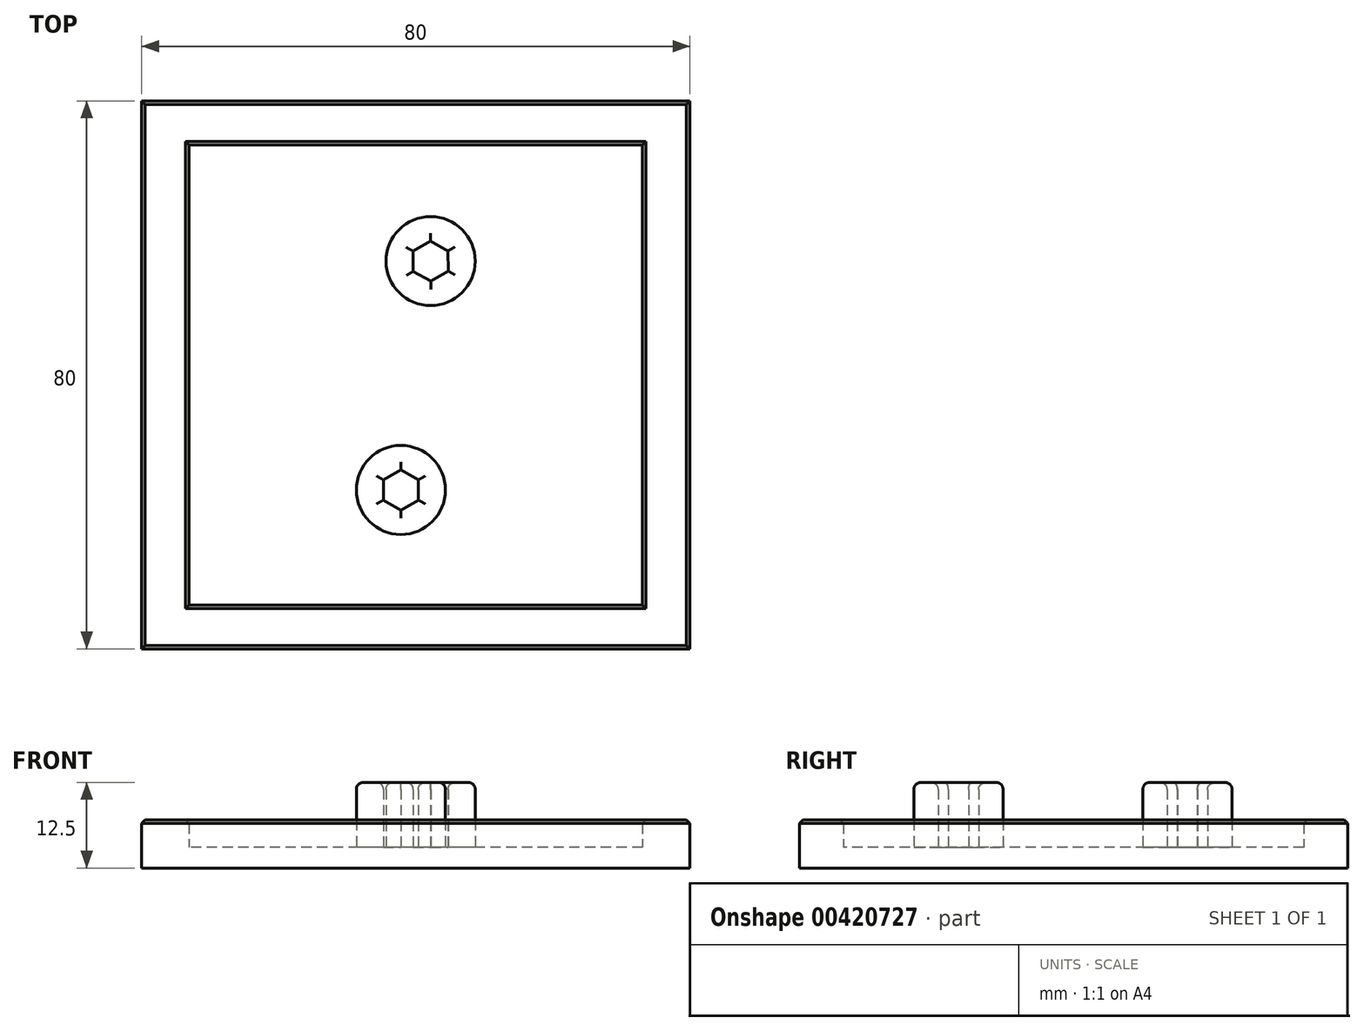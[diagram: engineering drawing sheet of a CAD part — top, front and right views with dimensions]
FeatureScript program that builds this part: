
annotation { "Feature Type Name" : "Feature", "Feature Type Description" : "" }
export const myFeature = defineFeature(function(context is Context, id is Id, definition is map)
    precondition{}
    {
        {
            var Q0;
            Q0=qCreatedBy(makeId("Top.planeOp"),FACE);
            var sketch = newSketch(context, id + "F0", { "sketchPlane" : qUnion([Q0])});
            skLineSegment(sketch, "E0.bottom", {"start": v(40, 40) * mm, "end": v(-40, 40) * mm});
            skLineSegment(sketch, "E0.top", {"start": v(40, -40) * mm, "end": v(-40, -40) * mm});
            skLineSegment(sketch, "E0.left", {"start": v(40, 40) * mm, "end": v(40, -40) * mm});
            skLineSegment(sketch, "E0.right", {"start": v(-40, 40) * mm, "end": v(-40, -40) * mm});
            skPoint(sketch, "E0.middle", {"position": v(0, 0) * mm});
            skCircle(sketch, "E1.cCircle", {"center": v(2.17, 16.62) * mm, "radius": 2.55 * mm, "construction": true});
            skLineSegment(sketch, "E1.0", {"start": v(2.15, 19.56) * mm, "end": v(4.7, 18.1) * mm});
            skLineSegment(sketch, "E1.1", {"start": v(4.7, 18.1) * mm, "end": v(4.73, 15.17) * mm});
            skLineSegment(sketch, "E1.2", {"start": v(4.73, 15.17) * mm, "end": v(2.2, 13.67) * mm});
            skLineSegment(sketch, "E1.3", {"start": v(2.2, 13.67) * mm, "end": v(-0.37, 15.12) * mm});
            skLineSegment(sketch, "E1.4", {"start": v(-0.37, 15.12) * mm, "end": v(-0.4, 18.07) * mm});
            skLineSegment(sketch, "E1.5", {"start": v(-0.4, 18.07) * mm, "end": v(2.15, 19.56) * mm});
            skPoint(sketch, "E1.0.midPoint", {"position": v(3.43, 18.84) * mm});
            skCircle(sketch, "E2", {"center": v(2.17, 16.62) * mm, "radius": 6.5 * mm});
            skCircle(sketch, "E3.cCircle", {"center": v(-2.17, -16.8) * mm, "radius": 2.55 * mm, "construction": true});
            skLineSegment(sketch, "E3.0", {"start": v(0.38, -15.33) * mm, "end": v(0.38, -18.27) * mm});
            skLineSegment(sketch, "E3.1", {"start": v(0.38, -18.27) * mm, "end": v(-2.17, -19.74) * mm});
            skLineSegment(sketch, "E3.2", {"start": v(-2.17, -19.74) * mm, "end": v(-4.72, -18.27) * mm});
            skLineSegment(sketch, "E3.3", {"start": v(-4.72, -18.27) * mm, "end": v(-4.72, -15.33) * mm});
            skLineSegment(sketch, "E3.4", {"start": v(-4.72, -15.33) * mm, "end": v(-2.17, -13.86) * mm});
            skLineSegment(sketch, "E3.5", {"start": v(-2.17, -13.86) * mm, "end": v(0.38, -15.33) * mm});
            skPoint(sketch, "E3.0.midPoint", {"position": v(0.38, -16.8) * mm});
            skCircle(sketch, "E4", {"center": v(-2.17, -16.8) * mm, "radius": 6.5 * mm});
            skSolve(sketch);
        }
        {
            var Q0;
            Q0=makeQuery(id+"F0.imprint","IMPRINT",FACE,{"disambiguationData":[TD([[makeQuery(id+"F0.imprint","IMPRINT",EDGE,{"derivedFrom":sQuery(id+"F0.wireOp",EDGE,"E0.bottom")}),1.0]])]});
            var Q1;
            Q1=makeQuery(id+"F0.imprint","IMPRINT",FACE,{"disambiguationData":[TD([[makeQuery(id+"F0.imprint","IMPRINT",EDGE,{"derivedFrom":sQuery(id+"F0.wireOp",EDGE,"E1.0")}),1.0]])]});
            var Q2;
            Q2=makeQuery(id+"F0.imprint","IMPRINT",FACE,{"disambiguationData":[TD([[makeQuery(id+"F0.imprint","IMPRINT",EDGE,{"derivedFrom":sQuery(id+"F0.wireOp",EDGE,"E1.0")}),-1.0]])]});
            var Q3;
            Q3=makeQuery(id+"F0.imprint","IMPRINT",FACE,{"disambiguationData":[TD([[makeQuery(id+"F0.imprint","IMPRINT",EDGE,{"derivedFrom":sQuery(id+"F0.wireOp",EDGE,"gQONg82r-pYZi-LkUd-rfeB-qmEZ9qJ01gSx")}),-1.0]])]});
            var Q4;
            Q4=makeQuery(id+"F0.imprint","IMPRINT",FACE,{"disambiguationData":[TD([[makeQuery(id+"F0.imprint","IMPRINT",EDGE,{"derivedFrom":sQuery(id+"F0.wireOp",EDGE,"gQONg82r-pYZi-LkUd-rfeB-qmEZ9qJ01gSx")}),1.0]])]});
            var Q5;
            Q5=makeQuery(id+"F0.imprint","IMPRINT",FACE,{"disambiguationData":[TD([[makeQuery(id+"F0.imprint","IMPRINT",EDGE,{"derivedFrom":sQuery(id+"F0.wireOp",EDGE,"rSCinz5W-PWQ1-Tyf3-0WCw-5ZFN2yuS5qdL")}),1.0]])]});
            var Q6;
            Q6=makeQuery(id+"F0.imprint","IMPRINT",FACE,{"disambiguationData":[TD([[makeQuery(id+"F0.imprint","IMPRINT",EDGE,{"derivedFrom":sQuery(id+"F0.wireOp",EDGE,"rSCinz5W-PWQ1-Tyf3-0WCw-5ZFN2yuS5qdL")}),-1.0]])]});
            var Q7;
            Q7=makeQuery(id+"F0.imprint","IMPRINT",FACE,{"disambiguationData":[TD([[makeQuery(id+"F0.imprint","IMPRINT",EDGE,{"derivedFrom":sQuery(id+"F0.wireOp",EDGE,"PcAE5poN-MP8w-SmH2-FwNS-jAMijU5FzXcH")}),1.0]])]});
            var Q8;
            Q8=makeQuery(id+"F0.imprint","IMPRINT",FACE,{"disambiguationData":[TD([[makeQuery(id+"F0.imprint","IMPRINT",EDGE,{"derivedFrom":sQuery(id+"F0.wireOp",EDGE,"E3.0")}),1.0]])]});
            var Q9;
            Q9=makeQuery(id+"F0.imprint","IMPRINT",FACE,{"disambiguationData":[TD([[makeQuery(id+"F0.imprint","IMPRINT",EDGE,{"derivedFrom":sQuery(id+"F0.wireOp",EDGE,"E3.0")}),-1.0]])]});
            extrude(context, id + "F1", {"entities" : qUnion([Q0, Q1, Q2, Q3, Q4, Q5, Q6, Q7, Q8, Q9]), "depth" : 3 * mm});
        }
        {
            var Q0;
            Q0=makeQuery(id+"F0.imprint","IMPRINT",FACE,{"disambiguationData":[TD([[makeQuery(id+"F0.imprint","IMPRINT",EDGE,{"derivedFrom":sQuery(id+"F0.wireOp",EDGE,"rSCinz5W-PWQ1-Tyf3-0WCw-5ZFN2yuS5qdL")}),-1.0]])]});
            var Q1;
            Q1=makeQuery(id+"F0.imprint","IMPRINT",FACE,{"disambiguationData":[TD([[makeQuery(id+"F0.imprint","IMPRINT",EDGE,{"derivedFrom":sQuery(id+"F0.wireOp",EDGE,"gQONg82r-pYZi-LkUd-rfeB-qmEZ9qJ01gSx")}),-1.0]])]});
            var Q2;
            Q2=makeQuery(id+"F0.imprint","IMPRINT",FACE,{"disambiguationData":[TD([[makeQuery(id+"F0.imprint","IMPRINT",EDGE,{"derivedFrom":sQuery(id+"F0.wireOp",EDGE,"E1.0")}),1.0]])]});
            var Q3;
            Q3=makeQuery(id+"F0.imprint","IMPRINT",FACE,{"disambiguationData":[TD([[makeQuery(id+"F0.imprint","IMPRINT",EDGE,{"derivedFrom":sQuery(id+"F0.wireOp",EDGE,"PcAE5poN-MP8w-SmH2-FwNS-jAMijU5FzXcH")}),1.0]])]});
            var Q4;
            Q4=makeQuery(id+"F0.imprint","IMPRINT",FACE,{"disambiguationData":[TD([[makeQuery(id+"F0.imprint","IMPRINT",EDGE,{"derivedFrom":sQuery(id+"F0.wireOp",EDGE,"E3.0")}),1.0]])]});
            extrude(context, id + "F2", {"entities" : qUnion([Q0, Q1, Q2, Q3, Q4]), "operationType" : NewBodyOperationType.ADD, "depth" : 12.5 * mm});
        }
        {
            var Q0;
            Q0=makeQuery(id+"F2.opExtrude","CAP_FACE",FACE,{"disambiguationData":[OSD([sQuery(id+"F0.wireOp",EDGE,"E1.0"),sQuery(id+"F0.wireOp",EDGE,"E1.1"),sQuery(id+"F0.wireOp",EDGE,"E1.2"),sQuery(id+"F0.wireOp",EDGE,"E1.3"),sQuery(id+"F0.wireOp",EDGE,"E1.4"),sQuery(id+"F0.wireOp",EDGE,"E1.5"),sQuery(id+"F0.wireOp",EDGE,"E2")])],"isStart":false});
            var Q1;
            Q1=makeQuery(id+"F2.opExtrude","CAP_FACE",FACE,{"disambiguationData":[OSD([sQuery(id+"F0.wireOp",EDGE,"E3.0"),sQuery(id+"F0.wireOp",EDGE,"E3.1"),sQuery(id+"F0.wireOp",EDGE,"E3.2"),sQuery(id+"F0.wireOp",EDGE,"E3.3"),sQuery(id+"F0.wireOp",EDGE,"E3.4"),sQuery(id+"F0.wireOp",EDGE,"E3.5"),sQuery(id+"F0.wireOp",EDGE,"E4")])],"isStart":false});
            fillet(context, id + "F3", {"entities" : qUnion([Q0, Q1]), "radius" : 1 * mm, "tangentPropagation" : true, "allowEdgeOverflow" : false});
        }
        {
            var Q0;
            {var subQ0=sQuery(id+"F0.wireOp",EDGE,"E0.left");var subQ1=sQuery(id+"F0.wireOp",EDGE,"E0.top");var subQ2=sQuery(id+"F0.wireOp",EDGE,"E0.right");var subQ3=sQuery(id+"F0.wireOp",EDGE,"E0.bottom");Q0=makeQuery(id+"F2.boolean.opBoolean","SPLIT",FACE,{"disambiguationData":[TD([makeQuery(id+"F1.opExtrude","SWEPT_FACE",FACE,{"disambiguationData":[OSD([subQ3])]})])],"derivedFrom":makeQuery(id+"F1.opExtrude","CAP_FACE",FACE,{"disambiguationData":[OSD([subQ3,subQ1,subQ0,subQ2])],"isStart":false})});}
            var sketch = newSketch(context, id + "F4", { "sketchPlane" : qUnion([Q0])});
            skLineSegment(sketch, "E5.bottom", {"start": v(33.1, 33.6) * mm, "end": v(-33.1, 33.6) * mm});
            skLineSegment(sketch, "E5.top", {"start": v(33.1, -33.6) * mm, "end": v(-33.1, -33.6) * mm});
            skLineSegment(sketch, "E5.left", {"start": v(33.1, 33.6) * mm, "end": v(33.1, -33.6) * mm});
            skLineSegment(sketch, "E5.right", {"start": v(-33.1, 33.6) * mm, "end": v(-33.1, -33.6) * mm});
            skPoint(sketch, "E5.middle", {"position": v(0, 0) * mm});
            skSolve(sketch);
        }
        {
            var Q0;
            Q0=makeQuery(id+"F4.imprint","IMPRINT",FACE,{"disambiguationData":[TD([[makeQuery(id+"F4.imprint","IMPRINT",EDGE,{"derivedFrom":sQuery(id+"F4.wireOp",EDGE,"E5.bottom")}),-1.0]])]});
            extrude(context, id + "F5", {"entities" : qUnion([Q0]), "operationType" : NewBodyOperationType.ADD, "depth" : 4 * mm});
        }
        {
            var Q0;
            Q0=makeQuery(id+"F5.opExtrude","CAP_FACE",FACE,{"disambiguationData":[OSD([sQuery(id+"F0.wireOp",EDGE,"E0.bottom"),sQuery(id+"F0.wireOp",EDGE,"E0.top"),sQuery(id+"F0.wireOp",EDGE,"E0.left"),sQuery(id+"F0.wireOp",EDGE,"E0.right"),sQuery(id+"F4.wireOp",EDGE,"E5.bottom"),sQuery(id+"F4.wireOp",EDGE,"E5.top"),sQuery(id+"F4.wireOp",EDGE,"E5.left"),sQuery(id+"F4.wireOp",EDGE,"E5.right")])],"isStart":false});
            chamfer(context, id + "F6", {"entities" : qUnion([Q0]), "width" : .5 * mm, "tangentPropagation" : true});
        }
    });
